# Revit family: Pantalla Modelo EL_ELVD130W
name_source: partatom
category: Luminarias
units: mm (PartAtom-declared; Revit-internal decimal feet)

## family parameters
Compartido = No
Corte con vacíos al cargar = No
Cota de conector redondo = Diámetro de uso
Origen de luz = No
Punto de cálculo de habitación = No
Se basa en plano de trabajo = Sí
Siempre vertical = No
Tipo de pieza = Normal

## types (4) — shared parameters
Comentarios de vataje = 100-240V
Espesor = 70 mm  [stored 0.229659 ft]
Fabricante = BRILLANT
Lámpara = SMD
Modulo = 600 mm  [stored 1.9685 ft]
Watt per fixture = 130
zero-valued in all types: Elevación por defecto

## per-type parameters (varying)
| type | Descripción | Modelo |
| Pantalla Modelo EL_ELVD130W.2 | PANTALLA MODELO EL 2, GABINETE PANTALLA LED AL AIRE LIBRE, CODIGO ELVD130W.2 MODELO EL2, PIXEL PITCH 2.8MM, RESOLUCION DEL PANEL 208X208DOTS, CANTIDAD/PANEL LED 43264 DOTS, CONFIGURACION DEL PIXEL SMD 3 EN 1, 900-1500 NITS, ACTUALIZACION 2000Hz, ESCALA DE GRISES 16BIT, AJUSTE DE BRILLO 256 NIVELES, CONTRASTE 1000:1, DIMENSION DEL PANEL 600X600X70MM, PANEL 0.36M2, PESO DEL PANEL 9KG, CONSUMO DE ENERGIA 130W, ANGULO DE VISUALIZACION 140 GRADOS 120 GRADOS, 2M DISTANCIA DE VISUALIZACION, PUNTO DE CONTROL 0.0002, DURACION DE LUCES (50% BRILLO) 50000 HORAS, TEMPERATURA DE FUNCIONAMIENTO -30C +40C, HUMEDAD RELATIVA 10-90%, IP 43/IP54 OPCIONAL, VOLTAJE AC 100-240V/50-60Hz, MODO DE ENTRADA COMO CORRIENTE CONSTANTE, SISTEMA OPERATIVO WINDOWS 2000/XP/VISTA/WINDOWS 7, TIPO DE SEÑAL AV, S-VIDEO, VGA, CVBS, HDMI, DVI, SDI, CONTROL DE DISTANCIA HSYV <100M. | ELVD130W.2 |
| Pantalla Modelo EL_ELVD130W.3 | PANTALLA MODELO EL 3, GABINETE PANTALLA LED AL AIRE LIBRE, CODIGO ELVD130W.3 MODELO EL3, PIXEL PITCH 3.7MM, RESOLUCION DEL PANEL 160X160DOTS, CANTIDAD/PANEL LED 25600 DOTS, CONFIGURACION DEL PIXEL SMD 3 EN 1, 900-1500 NITS, ACTUALIZACION 2000Hz, ESCALA DE GRISES 16BIT, AJUSTE DE BRILLO 256 NIVELES, CONTRASTE 1000:1, DIMENSION DEL PANEL 600X600X70MM, PANEL 0.36M2, PESO DEL PANEL 9KG, CONSUMO DE ENERGIA 130W, ANGULO DE VISUALIZACION 140 GRADOS 120 GRADOS, 3M DISTANCIA DE VISUALIZACION, PUNTO DE CONTROL 0.0002, DURACION DE LUCES (50% BRILLO) 50000 HORAS, TEMPERATURA DE FUNCIONAMIENTO -30C +40C, HUMEDAD RELATIVA 10-90%, IP 43/IP54 OPCIONAL, VOLTAJE AC 100-240V/50-60Hz, MODO DE ENTRADA COMO CORRIENTE CONSTANTE, SISTEMA OPERATIVO WINDOWS 2000/XP/VISTA/WINDOWS 7, TIPO DE SEÑAL AV, S-VIDEO, VGA, CVBS, HDMI, DVI, SDI, CONTROL DE DISTANCIA HSYV <100M. | ELVD130W.3 |
| Pantalla Modelo EL_ELVD130W.4 | PANTALLA MODELO EL 4, GABINETE PANTALLA LED AL AIRE LIBRE, CODIGO ELVD130W.4 MODELO EL4, PIXEL PITCH 4.6MM, RESOLUCION DEL PANEL 128X128DOTS, CANTIDAD/PANEL LED 16384 DOTS, CONFIGURACION DEL PIXEL SMD 3 EN 1, 900-1500 NITS, ACTUALIZACION 2000Hz, ESCALA DE GRISES 16BIT, AJUSTE DE BRILLO 256 NIVELES, CONTRASTE 1000:1, DIMENSION DEL PANEL 600X600X70MM, PANEL 0.36M2, PESO DEL PANEL 9KG, CONSUMO DE ENERGIA 130W, ANGULO DE VISUALIZACION 140 GRADOS 120 GRADOS, 4M DISTANCIA DE VISUALIZACION, PUNTO DE CONTROL 0.0002, DURACION DE LUCES (50% BRILLO) 50000 HORAS, TEMPERATURA DE FUNCIONAMIENTO -30C +40C, HUMEDAD RELATIVA 10-90%, IP 43/IP54 OPCIONAL, VOLTAJE AC 100-240V/50-60Hz, MODO DE ENTRADA COMO CORRIENTE CONSTANTE, SISTEMA OPERATIVO WINDOWS 2000/XP/VISTA/WINDOWS 7, TIPO DE SEÑAL AV, S-VIDEO, VGA, CVBS, HDMI, DVI, SDI, CONTROL DE DISTANCIA HSYV <100M. | ELVD130W.4 |
| Pantalla Modelo EL_ELVD130W.6 | PANTALLA MODELO EL 6, GABINETE PANTALLA LED AL AIRE LIBRE, CODIGO ELVD130W.6 MODELO EL6, PIXEL PITCH 6.2MM, RESOLUCION DEL PANEL 96X96DOTS, CANTIDAD/PANEL LED 9216DOTS, CONFIGURACION DEL PIXEL SMD 3 EN 1, 5000-6000 NITS, ACTUALIZACION 2000Hz, ESCALA DE GRISES 16BIT, AJUSTE DE BRILLO 256 NIVELES, CONTRASTE 1000:1, DIMENSION DEL PANEL 600X600X70MM, PANEL 0.36M2, PESO DEL PANEL 10KG, CONSUMO DE ENERGIA 130W, ANGULO DE VISUALIZACION 140 GRADOS 120 GRADOS, 6M DISTANCIA DE VISUALIZACION, PUNTO DE CONTROL 0.0002, DURACION DE LUCES (50% BRILLO) 50000 HORAS, TEMPERATURA DE FUNCIONAMIENTO -30C +40C, HUMEDAD RELATIVA 10-90%, IP 65, VOLTAJE AC 100-240V/50-60Hz, MODO DE ENTRADA COMO CORRIENTE CONSTANTE, SISTEMA OPERATIVO WINDOWS 2000/XP/VISTA/WINDOWS 7, TIPO DE SEÑAL AV, S-VIDEO, VGA, CVBS, HDMI, DVI, SDI, CONTROL DE DISTANCIA HSYV <100M. | ELVD130W.6 |

note: [stored X ft] marks values corroborated as IEEE doubles in the binary element streams (Revit-internal decimal feet)

## geometry (parser evidence)
native form markers: Blend x2
no freeform markers — native parametric forms only
